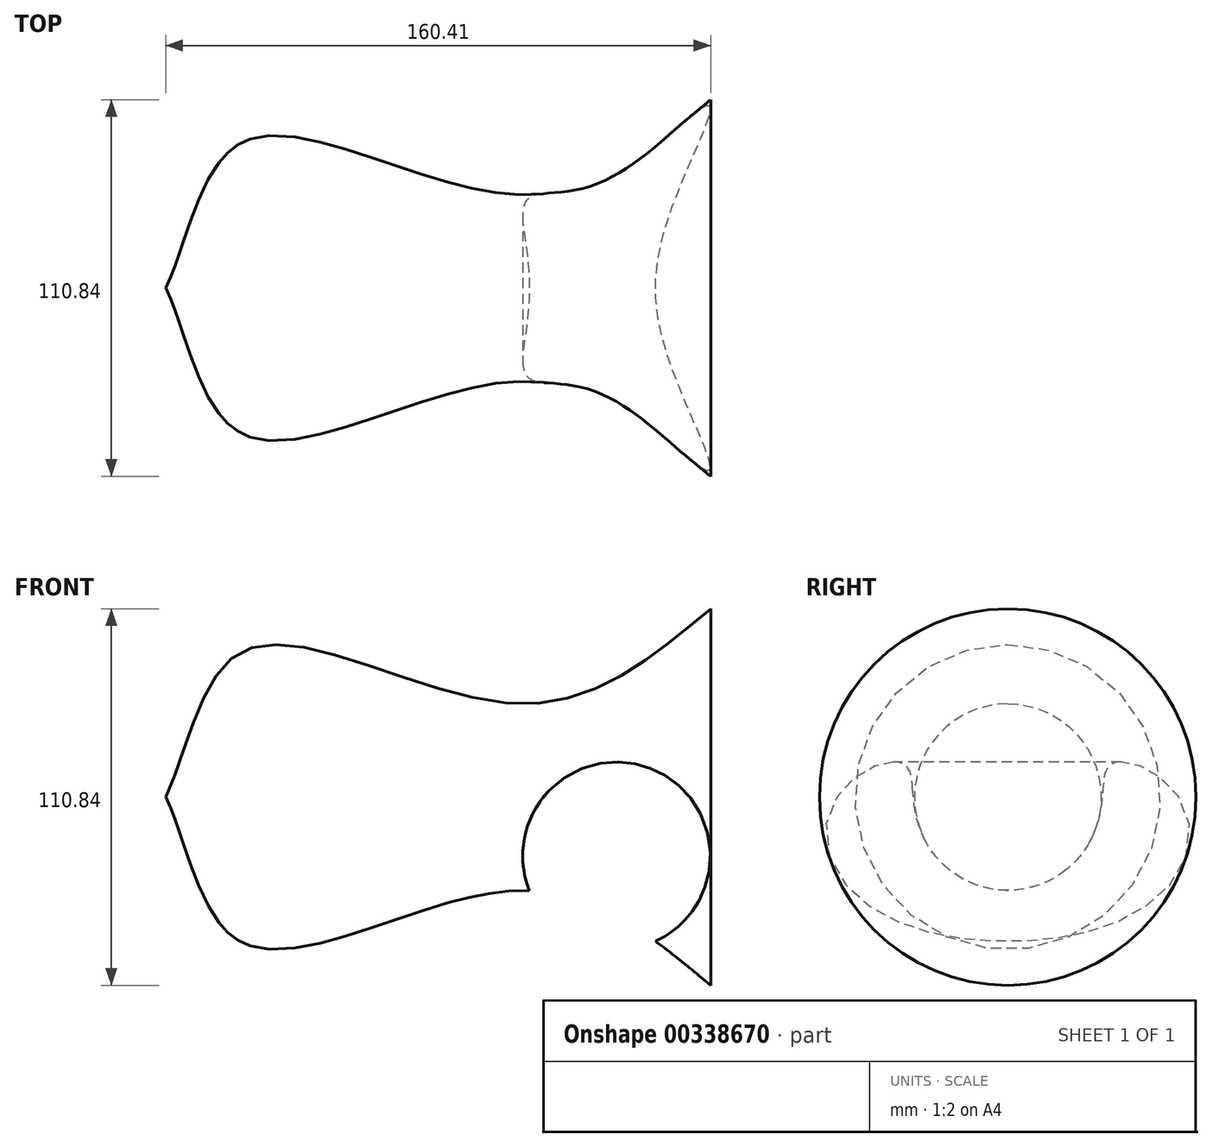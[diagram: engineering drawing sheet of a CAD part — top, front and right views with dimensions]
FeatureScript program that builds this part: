
annotation { "Feature Type Name" : "Feature", "Feature Type Description" : "" }
export const myFeature = defineFeature(function(context is Context, id is Id, definition is map)
    precondition{}
    {
        {
            var Q0;
            Q0=qCreatedBy(makeId("Front.planeOp"),FACE);
            var sketch = newSketch(context, id + "F0", { "sketchPlane" : qUnion([Q0])});
            skFitSpline(sketch, "E0", {"points": [v(-160.41, 0) * mm, v(-136.89, 43.34) * mm, v(-56.44, 27.47) * mm, v(0, 55.42) * mm], "startDerivative": vector(67.25, 134.58) * mm, "endDerivative": vector(137.42, 111.6) * mm});
            skLineSegment(sketch, "E1", {"start": v(0, 55.42) * mm, "end": v(0, 0) * mm});
            skLineSegment(sketch, "E2", {"start": v(0, 0) * mm, "end": v(-160.41, 0) * mm});
            skSolve(sketch);
        }
        {
            var Q0;
            Q0=makeQuery(id+"F0.imprint","IMPRINT",FACE,{"disambiguationData":[TD([[makeQuery(id+"F0.imprint","IMPRINT",EDGE,{"derivedFrom":sQuery(id+"F0.wireOp",EDGE,"E0")}),-1.0]])]});
            var Q1;
            Q1=sQuery(id+"F0.wireOp",EDGE,"E2");
            revolve(context, id + "F1", {"entities" : qUnion([Q0]), "axis" : qUnion([Q1]), "revolveType" : RevolveType.FULL});
        }
        {
            var Q0;
            Q0=qCreatedBy(makeId("Front.planeOp"),FACE);
            var sketch = newSketch(context, id + "F2", { "sketchPlane" : qUnion([Q0])});
            skCircle(sketch, "E3", {"center": v(-27.71, -17.29) * mm, "radius": 27.62 * mm});
            skSolve(sketch);
        }
        {
            var Q0;
            Q0=makeQuery(id+"F2.imprint","IMPRINT",FACE,{"disambiguationData":[TD([[makeQuery(id+"F2.imprint","IMPRINT",EDGE,{"derivedFrom":sQuery(id+"F2.wireOp",EDGE,"E3")}),1.0]])]});
            extrude(context, id + "F3", {"entities" : qUnion([Q0]), "operationType" : NewBodyOperationType.REMOVE, "endBound" : BoundingType.THROUGH_ALL, "oppositeDirection" : true, "depth" : 25.4 * mm, "hasSecondDirection" : true, "secondDirectionBound" : SecondDirectionBoundingType.THROUGH_ALL, "secondDirectionOppositeDirection" : false, "secondDirectionDepth" : 25.4 * mm});
        }
    });
